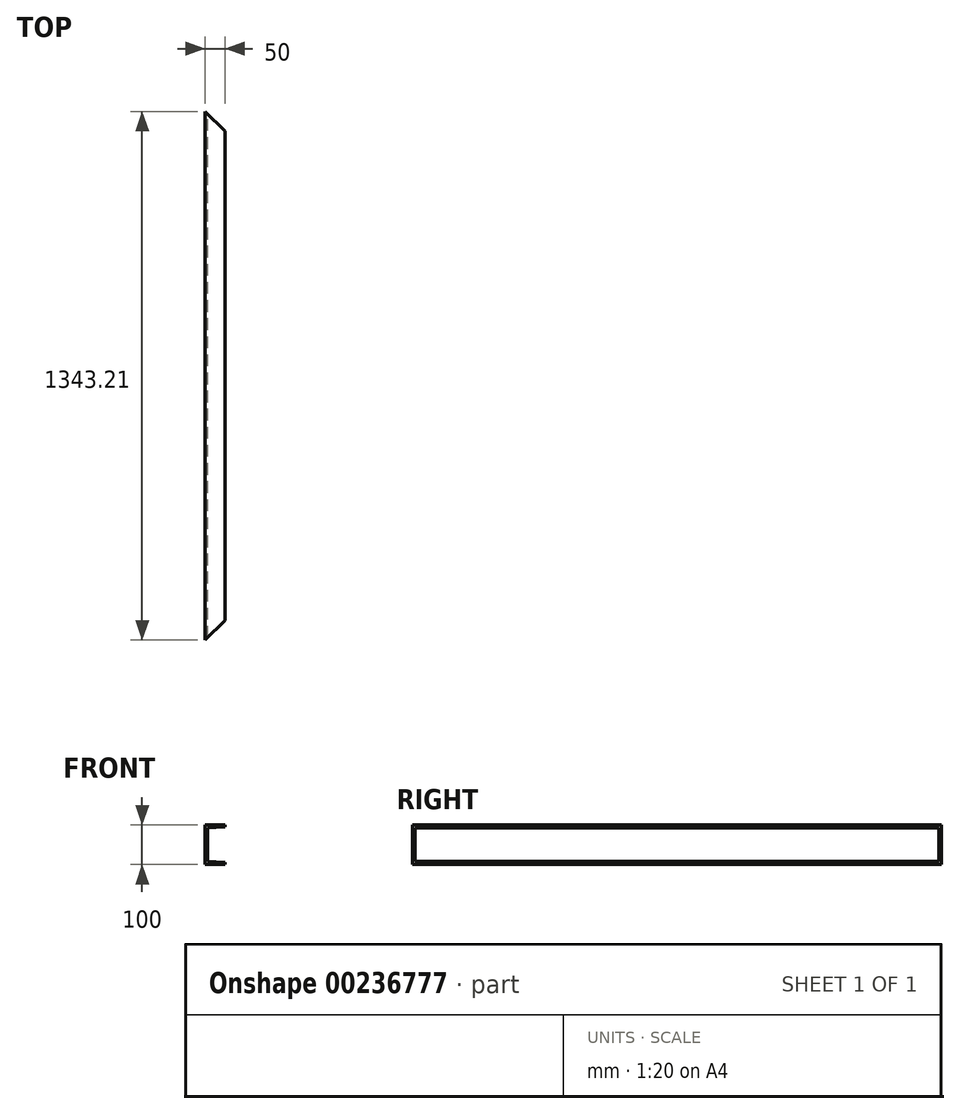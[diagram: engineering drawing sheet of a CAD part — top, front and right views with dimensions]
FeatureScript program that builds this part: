
annotation { "Feature Type Name" : "Feature", "Feature Type Description" : "" }
export const myFeature = defineFeature(function(context is Context, id is Id, definition is map)
    precondition{}
    {
        {
            var Q0;
            Q0=qCreatedBy(makeId("Front.planeOp"),FACE);
            var sketch = newSketch(context, id + "F0", { "sketchPlane" : qUnion([Q0])});
            skLineSegment(sketch, "E0.bottom", {"start": v(0, 0) * mm, "end": v(50, 0) * mm});
            skLineSegment(sketch, "E0.top", {"start": v(0, 100) * mm, "end": v(50, 100) * mm});
            skLineSegment(sketch, "E0.left", {"start": v(0, 0) * mm, "end": v(0, 100) * mm});
            skLineSegment(sketch, "E0.right", {"start": v(50, 0) * mm, "end": v(50, 5) * mm});
            skLineSegment(sketch, "E1.left", {"start": v(4.68, 71.03) * mm, "end": v(4.68, 71.03) * mm});
            skLineSegment(sketch, "E1.right", {"start": v(12.2, 71.03) * mm, "end": v(12.2, 71.03) * mm});
            skLineSegment(sketch, "E2", {"start": v(6, 8.46) * mm, "end": v(50, 5) * mm});
            skLineSegment(sketch, "E3", {"start": v(6, 8.46) * mm, "end": v(6, 93.46) * mm});
            skLineSegment(sketch, "E4", {"start": v(6, 93.46) * mm, "end": v(50, 95) * mm});
            skLineSegment(sketch, "E5.trimOffspring", {"start": v(50, 95) * mm, "end": v(50, 100) * mm});
            skSolve(sketch);
        }
        {
            var Q0;
            Q0=makeQuery(id+"F0.imprint","IMPRINT",FACE,{"disambiguationData":[TD([[makeQuery(id+"F0.imprint","IMPRINT",EDGE,{"derivedFrom":sQuery(id+"F0.wireOp",EDGE,"E0.bottom")}),1.0]])]});
            extrude(context, id + "F1", {"entities" : qUnion([Q0]), "depth" : (1500 - 156.79) * mm, "offsetDistance" : 25 * mm});
        }
        {
            var Q0;
            Q0=qCreatedBy(makeId("Top.planeOp"),FACE);
            var sketch = newSketch(context, id + "F2", { "sketchPlane" : qUnion([Q0])});
            skLineSegment(sketch, "E6", {"start": v(0, 52.26) * mm, "end": v(87.16, 52.26) * mm});
            skLineSegment(sketch, "E7", {"start": v(87.16, 52.26) * mm, "end": v(87.16, -87.16) * mm});
            skLineSegment(sketch, "E8", {"start": v(87.16, -87.16) * mm, "end": v(0, 0) * mm});
            skLineSegment(sketch, "E9", {"start": v(0, 0) * mm, "end": v(0, 52.26) * mm});
            skPoint(sketch, "E10.orphan", {"position": v(-38.59, 52.26) * mm});
            skLineSegment(sketch, "E11", {"start": v(0, -1353.21) * mm, "end": v(0, -1343.21) * mm});
            skLineSegment(sketch, "E12", {"start": v(0, -1343.21) * mm, "end": v(98.87, -1244.35) * mm});
            skLineSegment(sketch, "E13", {"start": v(98.87, -1244.35) * mm, "end": v(98.87, -1353.21) * mm});
            skLineSegment(sketch, "E14", {"start": v(98.87, -1353.21) * mm, "end": v(0, -1353.21) * mm});
            skSolve(sketch);
        }
        {
            var Q0;
            Q0=qSketchRegion(id+"F2",true);
            var Q1;
            Q1=makeQuery(id+"F1.opExtrude","SWEPT_FACE",FACE,{"disambiguationData":[OSD([sQuery(id+"F0.wireOp",EDGE,"E0.top")])]});
            extrude(context, id + "F3", {"entities" : qUnion([Q0, Q1]), "operationType" : NewBodyOperationType.REMOVE, "depth" : 110 * mm, "offsetDistance" : 25 * mm});
        }
    });
